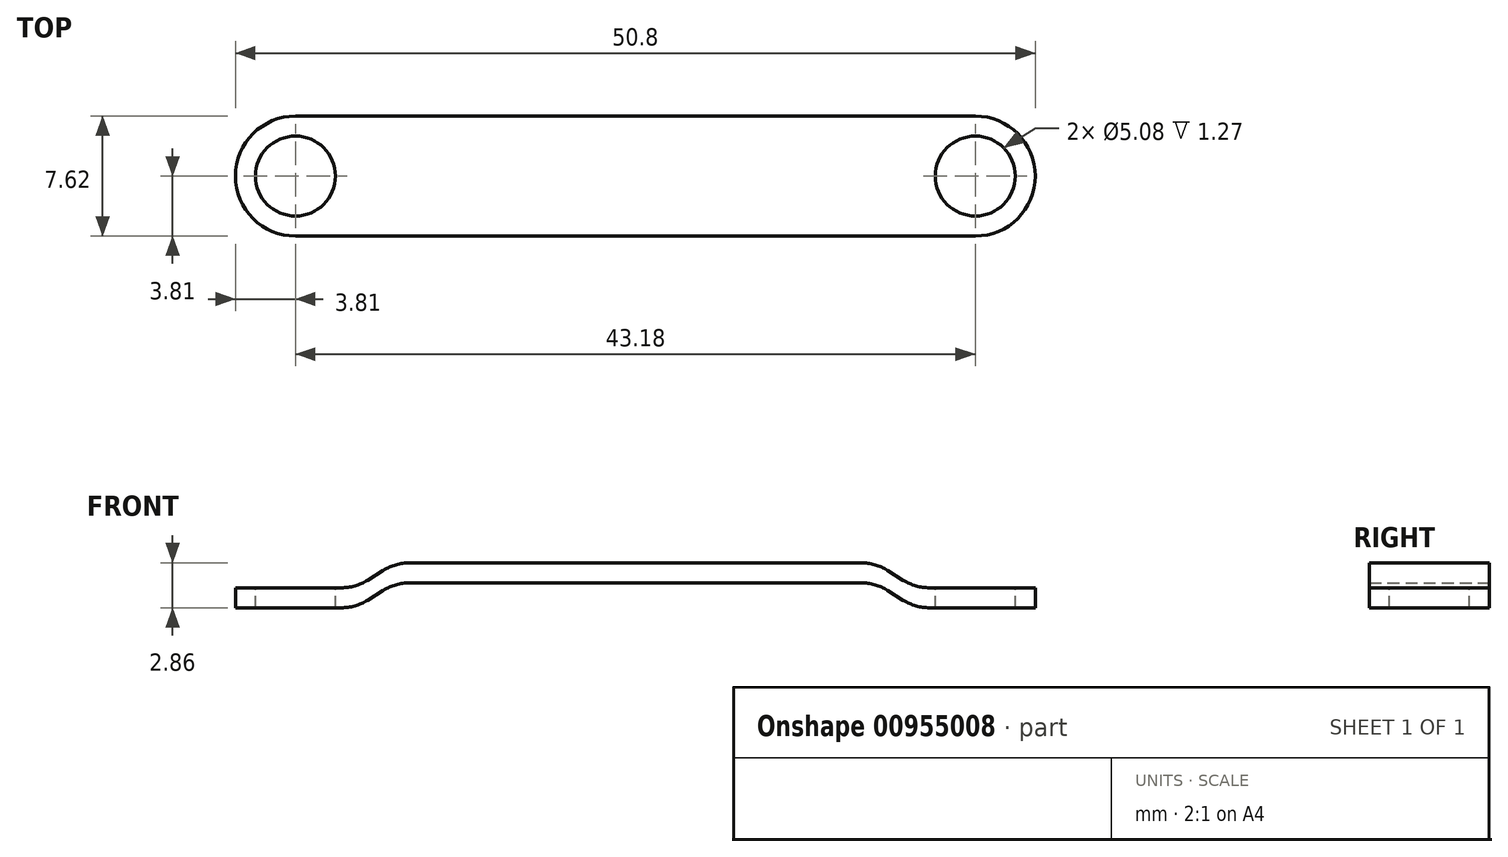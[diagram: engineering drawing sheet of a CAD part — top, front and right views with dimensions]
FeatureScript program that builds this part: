
annotation { "Feature Type Name" : "Feature", "Feature Type Description" : "" }
export const myFeature = defineFeature(function(context is Context, id is Id, definition is map)
    precondition{}
    {
        {
            var Q0;
            Q0=qCreatedBy(makeId("Top.planeOp"),FACE);
            var sketch = newSketch(context, id + "F0", { "sketchPlane" : qUnion([Q0])});
            skLineSegment(sketch, "E0", {"start": v(-21.59, 0) * mm, "end": v(21.59, 0) * mm, "construction": true});
            skPoint(sketch, "E1", {"position": v(0, 0) * mm});
            skCircle(sketch, "E2", {"center": v(-21.59, 0) * mm, "radius": 2.54 * mm});
            skCircle(sketch, "E3", {"center": v(21.59, 0) * mm, "radius": 2.54 * mm});
            skCircle(sketch, "E4", {"center": v(-21.59, 0) * mm, "radius": 3.81 * mm});
            skCircle(sketch, "E5", {"center": v(21.59, 0) * mm, "radius": 3.81 * mm});
            skSolve(sketch);
        }
        {
            var Q0;
            Q0=qCreatedBy(makeId("Front.planeOp"),FACE);
            var sketch = newSketch(context, id + "F1", { "sketchPlane" : qUnion([Q0])});
            skLineSegment(sketch, "E6.0", {"start": v(18.7, 0) * mm, "end": v(25.4, 0) * mm, "construction": true});
            skLineSegment(sketch, "E6.1", {"start": v(-25.4, 0) * mm, "end": v(-18.7, 0) * mm, "construction": true});
            skLineSegment(sketch, "E7", {"start": v(-25.4, 0) * mm, "end": v(-25.4, 1.27) * mm});
            skLineSegment(sketch, "E8", {"start": v(-25.4, 1.27) * mm, "end": v(-18.7, 1.27) * mm});
            skLineSegment(sketch, "E9", {"start": v(-17, 1.75) * mm, "end": v(-16.01, 2.37) * mm});
            skLineSegment(sketch, "E10", {"start": v(-14.33, 2.86) * mm, "end": v(14.33, 2.86) * mm});
            skLineSegment(sketch, "E11", {"start": v(16.01, 2.37) * mm, "end": v(17, 1.75) * mm});
            skLineSegment(sketch, "E12", {"start": v(18.7, 1.27) * mm, "end": v(25.4, 1.27) * mm});
            skLineSegment(sketch, "E13", {"start": v(25.4, 1.27) * mm, "end": v(25.4, 0) * mm});
            skPoint(sketch, "E14", {"position": v(0, 2.86) * mm});
            skLineSegment(sketch, "E15", {"start": v(-17, 0.48) * mm, "end": v(-16.01, 1.1) * mm});
            skLineSegment(sketch, "E16", {"start": v(-14.33, 1.59) * mm, "end": v(14.33, 1.59) * mm});
            skLineSegment(sketch, "E17", {"start": v(16.01, 1.1) * mm, "end": v(17, 0.48) * mm});
            skPoint(sketch, "E18.visualSharp", {"position": v(-15.24, 2.86) * mm});
            skArc(sketch, "E18.filletArc", {"start": v(-14.33, 2.86) * mm, "mid": v(-15.2, 2.73) * mm, "end": v(-16.01, 2.37) * mm});
            skPoint(sketch, "E19.visualSharp", {"position": v(-15.24, 1.59) * mm});
            skArc(sketch, "E19.filletArc", {"start": v(-14.33, 1.59) * mm, "mid": v(-15.2, 1.46) * mm, "end": v(-16.01, 1.1) * mm});
            skPoint(sketch, "E20.visualSharp", {"position": v(-17.78, 1.27) * mm});
            skArc(sketch, "E20.filletArc", {"start": v(-18.7, 1.27) * mm, "mid": v(-17.82, 1.4) * mm, "end": v(-17, 1.75) * mm});
            skPoint(sketch, "E21.visualSharp", {"position": v(-17.78, 0) * mm});
            skArc(sketch, "E21.filletArc", {"start": v(-18.7, 0) * mm, "mid": v(-17.82, 0.12) * mm, "end": v(-17, 0.48) * mm});
            skPoint(sketch, "E22.visualSharp", {"position": v(15.24, 2.86) * mm});
            skArc(sketch, "E22.filletArc", {"start": v(16.01, 2.37) * mm, "mid": v(15.2, 2.73) * mm, "end": v(14.33, 2.86) * mm});
            skPoint(sketch, "E23.visualSharp", {"position": v(15.24, 1.59) * mm});
            skArc(sketch, "E23.filletArc", {"start": v(16.01, 1.1) * mm, "mid": v(15.2, 1.46) * mm, "end": v(14.33, 1.59) * mm});
            skPoint(sketch, "E24.visualSharp", {"position": v(17.78, 1.27) * mm});
            skArc(sketch, "E24.filletArc", {"start": v(17, 1.75) * mm, "mid": v(17.82, 1.4) * mm, "end": v(18.7, 1.27) * mm});
            skPoint(sketch, "E25.visualSharp", {"position": v(17.78, 0) * mm});
            skArc(sketch, "E25.filletArc", {"start": v(17, 0.48) * mm, "mid": v(17.82, 0.12) * mm, "end": v(18.7, 0) * mm});
            skLineSegment(sketch, "E26", {"start": v(18.7, 0) * mm, "end": v(25.4, 0) * mm});
            skLineSegment(sketch, "E27", {"start": v(-25.4, 0) * mm, "end": v(-18.7, 0) * mm});
            skSolve(sketch);
        }
        {
            var Q0;
            Q0 = qSketchRegion(id + "F1", true);
            extrude(context, id + "F2", {"entities" : qUnion([Q0]), "depth" : 7.62 * mm, "offsetDistance" : 25.4 * mm, "symmetric" : true});
        }
        {
            var Q0;
            Q0=sQuery(id+"F0.wireOp",VERTEX,"E0.start");
            var Q1;
            Q1=sQuery(id+"F0.wireOp",VERTEX,"E0.end");
            var Q2;
            Q2=makeQuery(id+"F2.opExtrude","SWEPT_BODY",BODY,{"disambiguationData":[OSD([sQuery(id+"F1.wireOp",EDGE,"E7"),sQuery(id+"F1.wireOp",EDGE,"E8"),sQuery(id+"F1.wireOp",EDGE,"E9"),sQuery(id+"F1.wireOp",EDGE,"E10"),sQuery(id+"F1.wireOp",EDGE,"E11"),sQuery(id+"F1.wireOp",EDGE,"E12"),sQuery(id+"F1.wireOp",EDGE,"E13"),sQuery(id+"F1.wireOp",EDGE,"E15"),sQuery(id+"F1.wireOp",EDGE,"E16"),sQuery(id+"F1.wireOp",EDGE,"E17"),sQuery(id+"F1.wireOp",EDGE,"E18.filletArc"),sQuery(id+"F1.wireOp",EDGE,"E19.filletArc"),sQuery(id+"F1.wireOp",EDGE,"E20.filletArc"),sQuery(id+"F1.wireOp",EDGE,"E21.filletArc"),sQuery(id+"F1.wireOp",EDGE,"E22.filletArc"),sQuery(id+"F1.wireOp",EDGE,"E23.filletArc"),sQuery(id+"F1.wireOp",EDGE,"E24.filletArc"),sQuery(id+"F1.wireOp",EDGE,"E25.filletArc"),sQuery(id+"F1.wireOp",EDGE,"E26"),sQuery(id+"F1.wireOp",EDGE,"E27")])]});
            hole(context, id + "F3", {"style" : HoleStyle.SIMPLE, "endStyle" : HoleEndStyle.BLIND, "oppositeDirection" : true, "holeDiameter" : 5.08 * mm, "majorDiameter" : 6.35 * mm, "holeDepth" : 3.8 * mm, "isTappedThrough" : true, "tappedDepth" : 3.17 * mm, "tapClearance" : 3, "locations" : qUnion([Q0, Q1]), "scope" : qUnion([Q2]), "startStyle" : HoleStartStyle.SKETCH});
        }
        {
            var Q0;
            Q0=makeQuery(id+"F2.opExtrude","CAP_EDGE",EDGE,{"disambiguationData":[OSD([sQuery(id+"F1.wireOp",EDGE,"E7")])],"isStart":false});
            var Q1;
            Q1=makeQuery(id+"F2.opExtrude","CAP_EDGE",EDGE,{"disambiguationData":[OSD([sQuery(id+"F1.wireOp",EDGE,"E7")])],"isStart":true});
            var Q2;
            Q2=makeQuery(id+"F2.opExtrude","CAP_EDGE",EDGE,{"disambiguationData":[OSD([sQuery(id+"F1.wireOp",EDGE,"E13")])],"isStart":false});
            var Q3;
            Q3=makeQuery(id+"F2.opExtrude","CAP_EDGE",EDGE,{"disambiguationData":[OSD([sQuery(id+"F1.wireOp",EDGE,"E13")])],"isStart":true});
            fillet(context, id + "F4", {"entities" : qUnion([Q0, Q1, Q2, Q3]), "tangentPropagation" : true, "radius" : 3.8 * mm, "defaultsChanged" : false, "vertexSettings" : [], "allowEdgeOverflow" : false});
        }
    });
